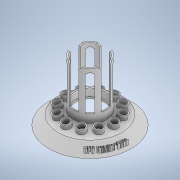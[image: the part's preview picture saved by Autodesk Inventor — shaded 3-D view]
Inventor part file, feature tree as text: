
AUTODESK INVENTOR PART (.ipt)
format: ipt  version: 2022.4 (Build 264492010, 492A)  size: 1,167,360 bytes
history: native  units: in
note: dims shown in document units (in); Inventor stores cm internally (conversion verified against a paired STEP export)
features: sketch x11, extrude x7, revolve x4, pattern_circular x4, plane x1, emboss x1, projected_geometry x1
ambient origin geometry x8: Origin, YZ Plane, XZ Plane, XY Plane, X Axis, Y Axis, Z Axis, Center Point
bodies: Solid1 (feature_tree)
feature tree (29):
  extrude  "Extrusion1"  Depth=0.0964in
  revolve  "Revolution1"  [1 undecoded]
  plane  "Work Plane1"
  extrude  "Extrusion3"  Depth=2.3622in
  extrude  "Extrusion4"  TaperAngle=0.0deg  [1 undecoded]
  extrude  "Extrusion5"  Depth=2.3622in
  revolve  "Revolution2"  [1 undecoded]
  pattern_circular  "Circular Pattern1"  Count=10  [1 undecoded]
  extrude  "Extrusion6"  Depth=0.315in
  pattern_circular  "Circular Pattern2"  Count=12 Angle=360.0deg
  extrude  "Extrusion7"  Depth=0.3937in
  revolve  "Revolution3"  [1 undecoded]
  revolve  "Revolution4"  [1 undecoded]
  pattern_circular  "Circular Pattern3"  [2 undecoded]
  extrude  "Extrusion8"  Depth=0.5512in
  pattern_circular  "Circular Pattern4"  [2 undecoded]
  emboss  "Emboss4"
  sketch  "Sketch1"  dims[d2=0.1969in d3=0.0in d8=0.0964in]
  sketch  "Sketch4"  dims[d9=90.0deg d10=0.5315in]
  sketch  "Sketch5"  dims[d11=2.5984in d12=2.3622in]
  sketch  "Sketch6"  dims[d13=0.1969in d14=0.0in d15=0.0in]
  sketch  "Sketch7"  dims[d16=2.5197in d17=2.3622in]
  sketch  "Sketch9"  dims[d18=0.0787in d19=0.0in d22=0.1181in d23=3.937in d24=0.0in]
  sketch  "Sketch13"  dims[d25=0.0591in d26=0.0in d35=0.315in]
  sketch  "Sketch14"  dims[d36=90.0deg d37=4.7244in d38=360.0deg]
  sketch  "Sketch16"  dims[d40=5.2756in d41=0.3937in]
  sketch  "Sketch17"  dims[d42=0.0825in d43=0.0in d44=0.0in]
  sketch  "Sketch20"  dims[d45=3.1496in d46=360.0deg d49=0.5906in d50=0.0in d51=0.5512in d52=4.5669in d53=5.0591in d54=4.626in d55=0.1575in d56=0.0in d57=0.0in d60=0.1969in d61=0.1969in d62=0.1969in d63=90.0deg d69=0.3937in d70=0.0825in d71=0.0in d72=90.0deg d73=0.0787in d74=0.2797in d75=0.0in d76=0.378in d77=4.7244in d78=360.0deg d81=0.5906in d82=0.0in d83=0.7874in d85=0.0in d86=0.0in d87=1.5748in d88=360.0deg d96=0.0787in d98=0.0787in d101=2.8275in d103=0.1969in d104=0.1969in d106=0.1969in d107=0.1969in d108=0.0787in d109=0.0in d111=0.2756in d68=0.0344in]
  projected_geometry  "Project Cut Edges1"
note: 10 required parameter values undecoded (feature->parameter linkage not recoverable at this tier; creation-order binding heuristic only, values carry confidence <= 0.55)